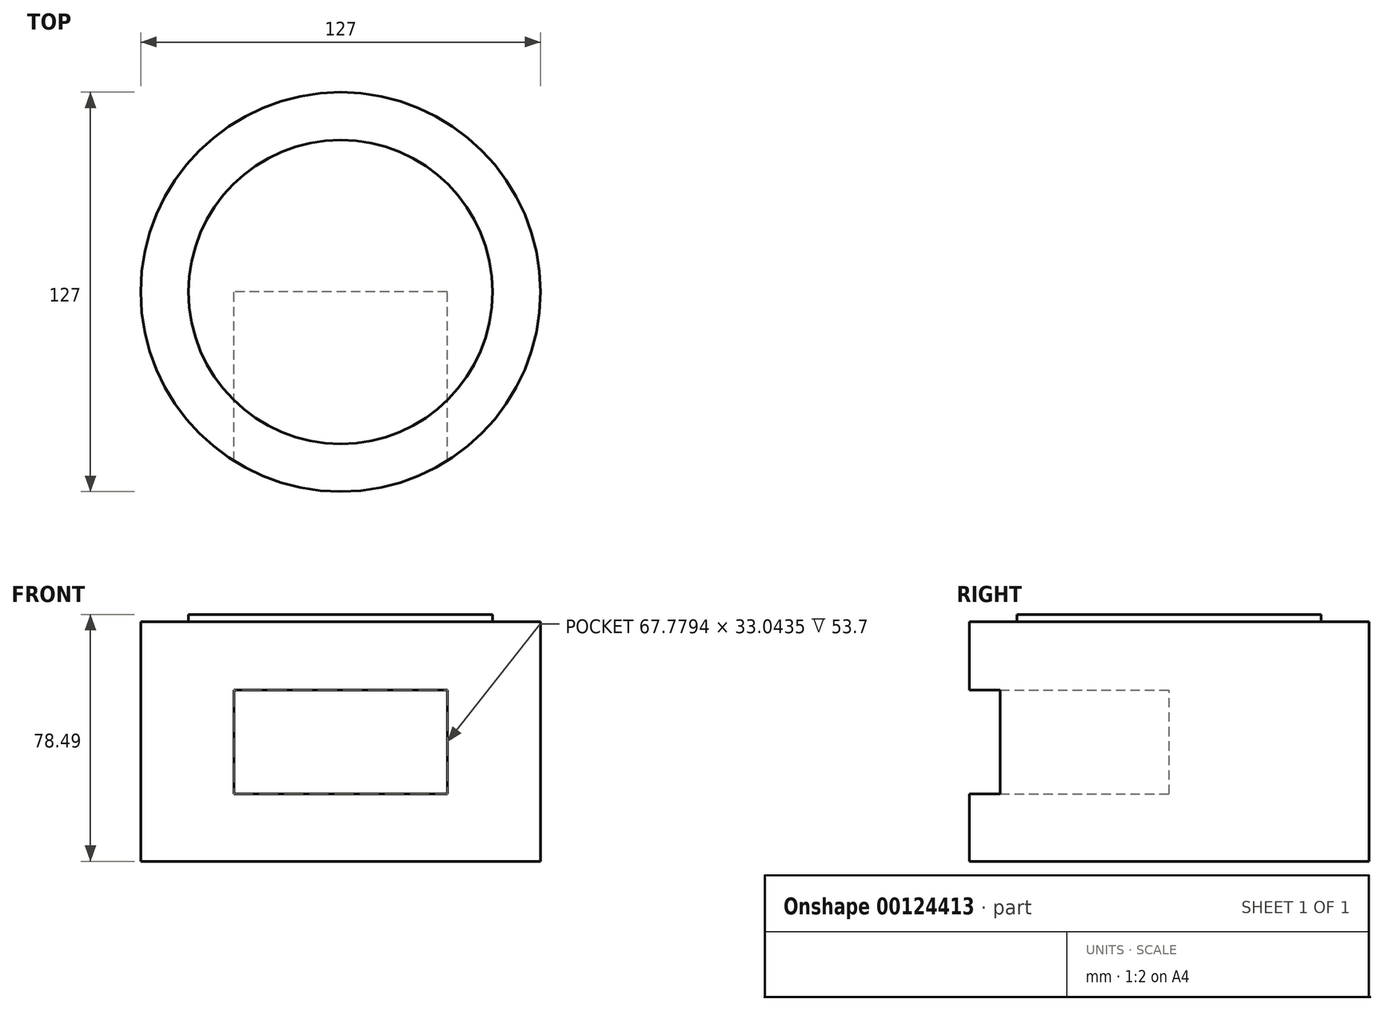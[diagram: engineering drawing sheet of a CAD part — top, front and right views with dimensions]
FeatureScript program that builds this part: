
annotation { "Feature Type Name" : "Feature", "Feature Type Description" : "" }
export const myFeature = defineFeature(function(context is Context, id is Id, definition is map)
    precondition{}
    {
        {
            var Q0;
            Q0=qCreatedBy(makeId("Top.planeOp"),FACE);
            var sketch = newSketch(context, id + "F0", { "sketchPlane" : qUnion([Q0])});
            skCircle(sketch, "E0", {"center": v(0, 0) * mm, "radius": 63.5 * mm});
            skSolve(sketch);
        }
        {
            var Q0;
            Q0=makeQuery(id+"F0.imprint","IMPRINT",FACE,{"disambiguationData":[TD([[makeQuery(id+"F0.imprint","IMPRINT",EDGE,{"derivedFrom":sQuery(id+"F0.wireOp",EDGE,"E0")}),1.0]])]});
            extrude(context, id + "F1", {"entities" : qUnion([Q0]), "depth" : 76.2 * mm});
        }
        {
            var Q0;
            Q0=makeQuery(id+"F1.opExtrude","CAP_FACE",FACE,{"disambiguationData":[OSD([sQuery(id+"F0.wireOp",EDGE,"E0")])],"isStart":false});
            var sketch = newSketch(context, id + "F2", { "sketchPlane" : qUnion([Q0])});
            skLineSegment(sketch, "E1", {"start": v(-63.5, 0) * mm, "end": v(63.5, 0) * mm});
            skSolve(sketch);
        }
        {
            var Q0;
            {var subQ0=sQuery(id+"F2.wireOp",EDGE,"E1");Q0=makeQuery(id+"F2.imprint","IMPRINT",FACE,{"disambiguationData":[TD([[makeQuery(id+"F2.imprint","IMPRINT",EDGE,{"derivedFrom":subQ0}),-1.0]])]});}
            var sketch = newSketch(context, id + "F3", { "sketchPlane" : qUnion([Q0])});
            skCircle(sketch, "E2", {"center": v(0, 0) * mm, "radius": 48.31 * mm});
            skSolve(sketch);
        }
        {
            var Q0;
            Q0 = qSketchRegion(id + "F3", true);
            extrude(context, id + "F4", {"entities" : qUnion([Q0]), "operationType" : NewBodyOperationType.ADD, "depth" : 2.3 * mm});
        }
        {
            var Q0;
            Q0=qCreatedBy(makeId("Front.planeOp"),FACE);
            var sketch = newSketch(context, id + "F5", { "sketchPlane" : qUnion([Q0])});
            skLineSegment(sketch, "E3.bottom", {"start": v(33.89, 21.35) * mm, "end": v(-33.89, 21.35) * mm});
            skLineSegment(sketch, "E3.top", {"start": v(33.89, 54.4) * mm, "end": v(-33.89, 54.4) * mm});
            skLineSegment(sketch, "E3.left", {"start": v(33.89, 21.35) * mm, "end": v(33.89, 54.4) * mm});
            skLineSegment(sketch, "E3.right", {"start": v(-33.89, 21.35) * mm, "end": v(-33.89, 54.4) * mm});
            skPoint(sketch, "E3.middle", {"position": v(0, 37.88) * mm});
            skSolve(sketch);
        }
        {
            var Q0;
            Q0 = qSketchRegion(id + "F5", true);
            extrude(context, id + "F6", {"entities" : qUnion([Q0]), "operationType" : NewBodyOperationType.REMOVE, "depth" : 127 * mm});
        }
    });
